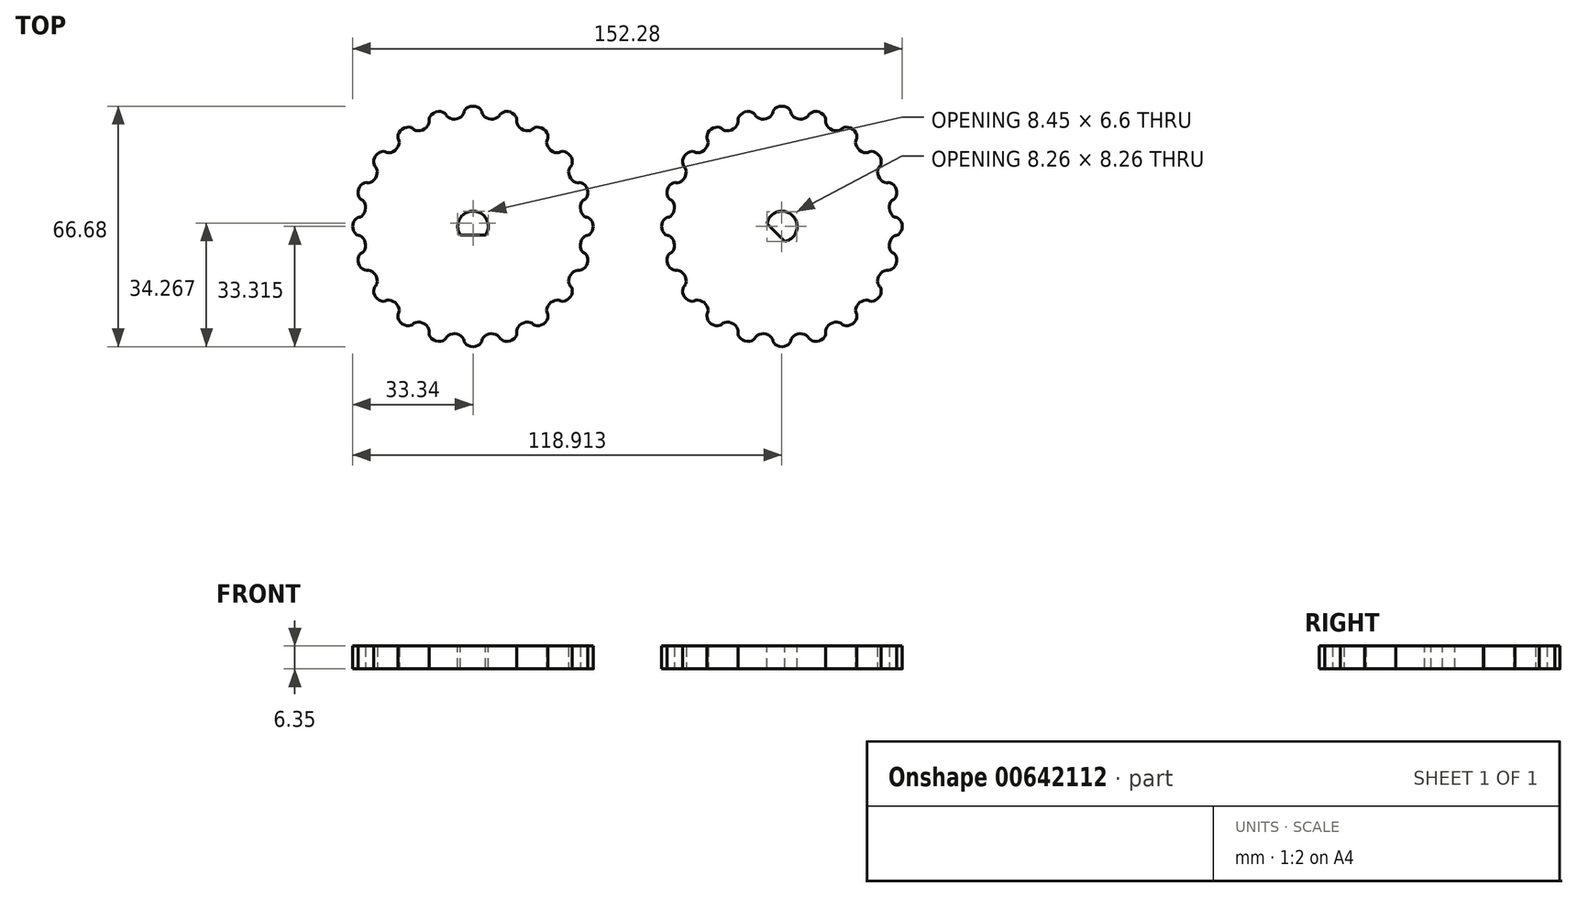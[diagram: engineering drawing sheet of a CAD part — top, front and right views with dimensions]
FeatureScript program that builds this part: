
annotation { "Feature Type Name" : "Feature", "Feature Type Description" : "" }
export const myFeature = defineFeature(function(context is Context, id is Id, definition is map)
    precondition{}
    {
        {
            assignVariable(context, id + "F0", {"name" : "PCD", "anyValue" : 2.5});
        }
        {
            assignVariable(context, id + "F1", {"name" : "SCD", "anyValue" : 1 / 16});
        }
        {
            assignVariable(context, id + "F2", {"name" : "Teeth", "anyValue" : .5 * getVariable(context, 'PCD') / getVariable(context, 'SCD')});
        }
        {
            var Q0;
            Q0=qCreatedBy(makeId("Top.planeOp"),FACE);
            var sketch = newSketch(context, id + "F3", { "sketchPlane" : qUnion([Q0])});
            skCircle(sketch, "E0", {"center": v(0, 0) * mm, "radius": 31.75 * mm, "construction": true});
            skCircle(sketch, "E1", {"center": v(0, 32.54) * mm, "radius": 0.8 * mm, "construction": true});
            skLineSegment(sketch, "E2", {"start": v(0, 33.34) * mm, "end": v(0, 32.54) * mm, "construction": true});
            skLineSegment(sketch, "E3", {"start": v(0, 0) * mm, "end": v(-4.84, 30.58) * mm, "construction": true});
            skCircle(sketch, "E4", {"center": v(-4.84, 30.58) * mm, "radius": 0.8 * mm, "construction": true});
            skLineSegment(sketch, "E5", {"start": v(0, 0) * mm, "end": v(0, 33.34) * mm, "construction": true});
            skCircle(sketch, "E6", {"center": v(0, 0) * mm, "radius": 33.34 * mm, "construction": true});
            skLineSegment(sketch, "E7", {"start": v(0, 0) * mm, "end": v(-2.5, 31.65) * mm, "construction": true});
            skLineSegment(sketch, "E8", {"start": v(0, 0) * mm, "end": v(-10.3, 31.7) * mm, "construction": true});
            skLineSegment(sketch, "E9", {"start": v(0, 0) * mm, "end": v(-7.41, 30.87) * mm, "construction": true});
            skCircle(sketch, "E10", {"center": v(-10.06, 30.95) * mm, "radius": 0.8 * mm, "construction": true});
            skCircle(sketch, "E11", {"center": v(-1.28, 32.52) * mm, "radius": 0.8 * mm, "construction": true});
            skCircle(sketch, "E12", {"center": v(-3.64, 30.74) * mm, "radius": 0.8 * mm, "construction": true});
            skLineSegment(sketch, "E13", {"start": v(-1.28, 32.52) * mm, "end": v(0, 0) * mm, "construction": true});
            skLineSegment(sketch, "E14", {"start": v(0, 0) * mm, "end": v(-3.64, 30.74) * mm, "construction": true});
            skLineSegment(sketch, "E15", {"start": v(-3.64, 30.74) * mm, "end": v(-2.85, 30.83) * mm, "construction": true});
            skLineSegment(sketch, "E16", {"start": v(-1.28, 32.52) * mm, "end": v(-2.07, 32.49) * mm, "construction": true});
            skPoint(sketch, "E17", {"position": v(-4.72, 29.8) * mm});
            skCircle(sketch, "E18", {"center": v(-6.04, 30.36) * mm, "radius": 0.8 * mm, "construction": true});
            skCircle(sketch, "E19", {"center": v(-8.83, 31.32) * mm, "radius": 0.8 * mm, "construction": true});
            skLineSegment(sketch, "E20", {"start": v(0, 0) * mm, "end": v(-6.04, 30.36) * mm, "construction": true});
            skLineSegment(sketch, "E21", {"start": v(0, 0) * mm, "end": v(-8.83, 31.32) * mm, "construction": true});
            skLineSegment(sketch, "E22", {"start": v(-6.04, 30.36) * mm, "end": v(-6.82, 30.2) * mm, "construction": true});
            skLineSegment(sketch, "E23", {"start": v(-8.83, 31.32) * mm, "end": v(-8.07, 31.54) * mm, "construction": true});
            skCircle(sketch, "E24", {"center": v(-0.64, 32.54) * mm, "radius": 0.8 * mm, "construction": true});
            skLineSegment(sketch, "E25", {"start": v(-0.64, 32.54) * mm, "end": v(0, 0) * mm, "construction": true});
            skCircle(sketch, "E26", {"center": v(-1.92, 32.49) * mm, "radius": 0.8 * mm, "construction": true});
            skLineSegment(sketch, "E27", {"start": v(-1.92, 32.49) * mm, "end": v(0, 0) * mm, "construction": true});
            skLineSegment(sketch, "E28", {"start": v(-0.64, 32.54) * mm, "end": v(-1.21, 33.09) * mm, "construction": true});
            skLineSegment(sketch, "E29", {"start": v(-1.92, 32.49) * mm, "end": v(-2.44, 31.9) * mm, "construction": true});
            skCircle(sketch, "E30", {"center": v(-3.03, 30.8) * mm, "radius": 0.8 * mm, "construction": true});
            skCircle(sketch, "E31", {"center": v(-4.24, 30.66) * mm, "radius": 0.8 * mm, "construction": true});
            skLineSegment(sketch, "E32", {"start": v(-3.03, 30.8) * mm, "end": v(0, 0) * mm, "construction": true});
            skLineSegment(sketch, "E33", {"start": v(-3.03, 30.8) * mm, "end": v(-2.53, 31.42) * mm, "construction": true});
            skLineSegment(sketch, "E34", {"start": v(-4.24, 30.66) * mm, "end": v(0, 0) * mm, "construction": true});
            skLineSegment(sketch, "E35", {"start": v(-4.24, 30.66) * mm, "end": v(-3.6, 30.19) * mm, "construction": true});
            skCircle(sketch, "E36", {"center": v(-5.44, 30.47) * mm, "radius": 0.8 * mm, "construction": true});
            skLineSegment(sketch, "E37", {"start": v(-5.44, 30.47) * mm, "end": v(0, 0) * mm, "construction": true});
            skLineSegment(sketch, "E38", {"start": v(-5.44, 30.47) * mm, "end": v(-5.9, 29.82) * mm, "construction": true});
            skCircle(sketch, "E39", {"center": v(-6.63, 30.24) * mm, "radius": 0.8 * mm, "construction": true});
            skCircle(sketch, "E40", {"center": v(-8.22, 31.49) * mm, "radius": 0.8 * mm, "construction": true});
            skCircle(sketch, "E41", {"center": v(-9.45, 31.14) * mm, "radius": 0.8 * mm, "construction": true});
            skLineSegment(sketch, "E42", {"start": v(-6.63, 30.24) * mm, "end": v(0, 0) * mm, "construction": true});
            skLineSegment(sketch, "E43", {"start": v(-6.63, 30.24) * mm, "end": v(-7.3, 30.66) * mm, "construction": true});
            skLineSegment(sketch, "E44", {"start": v(-8.22, 31.49) * mm, "end": v(0, 0) * mm, "construction": true});
            skLineSegment(sketch, "E45", {"start": v(-9.45, 31.14) * mm, "end": v(0, 0) * mm, "construction": true});
            skLineSegment(sketch, "E46", {"start": v(-8.22, 31.49) * mm, "end": v(-7.53, 31.09) * mm, "construction": true});
            skLineSegment(sketch, "E47", {"start": v(-9.45, 31.14) * mm, "end": v(-9.07, 31.84) * mm, "construction": true});
            skSolve(sketch);
        }
        {
            var Q0;
            Q0=qCreatedBy(makeId("Top.planeOp"),FACE);
            var sketch = newSketch(context, id + "F4", { "sketchPlane" : qUnion([Q0])});
            skPoint(sketch, "E48.0", {"position": v(0, 33.34) * mm});
            skPoint(sketch, "E48.1", {"position": v(-1.21, 33.09) * mm});
            skPoint(sketch, "E48.2", {"position": v(-2.07, 32.49) * mm});
            skPoint(sketch, "E48.3", {"position": v(-2.44, 31.9) * mm});
            skPoint(sketch, "E48.4", {"position": v(-2.5, 31.65) * mm});
            skPoint(sketch, "E48.5", {"position": v(-2.53, 31.42) * mm});
            skPoint(sketch, "E48.6", {"position": v(-2.85, 30.83) * mm});
            skPoint(sketch, "E48.7", {"position": v(-3.6, 30.19) * mm});
            skPoint(sketch, "E48.8", {"position": v(-4.72, 29.8) * mm});
            skPoint(sketch, "E48.9", {"position": v(-5.9, 29.82) * mm});
            skPoint(sketch, "E48.10", {"position": v(-6.82, 30.2) * mm});
            skPoint(sketch, "E48.11", {"position": v(-7.3, 30.66) * mm});
            skPoint(sketch, "E48.12", {"position": v(-7.41, 30.87) * mm});
            skPoint(sketch, "E48.13", {"position": v(-7.53, 31.09) * mm});
            skPoint(sketch, "E48.14", {"position": v(-8.07, 31.54) * mm});
            skPoint(sketch, "E48.15", {"position": v(-9.07, 31.84) * mm});
            skPoint(sketch, "E48.16", {"position": v(-10.3, 31.7) * mm});
            skLineSegment(sketch, "E49.0", {"start": v(0, 0) * mm, "end": v(0, 33.34) * mm});
            skLineSegment(sketch, "E49.1", {"start": v(0, 0) * mm, "end": v(-4.84, 30.58) * mm, "construction": true});
            skLineSegment(sketch, "E50.0", {"start": v(0, 0) * mm, "end": v(-10.3, 31.7) * mm});
            skPoint(sketch, "E51.1.1", {"position": v(-11.38, 31.1) * mm});
            skPoint(sketch, "E51.1.2", {"position": v(-12, 30.26) * mm});
            skPoint(sketch, "E51.1.3", {"position": v(-12.18, 29.58) * mm});
            skPoint(sketch, "E51.1.4", {"position": v(-12.15, 29.33) * mm});
            skPoint(sketch, "E51.1.5", {"position": v(-12.12, 29.1) * mm});
            skPoint(sketch, "E51.1.6", {"position": v(-12.24, 28.45) * mm});
            skPoint(sketch, "E51.1.7", {"position": v(-12.76, 27.6) * mm});
            skPoint(sketch, "E51.1.8", {"position": v(-13.7, 26.87) * mm});
            skPoint(sketch, "E51.1.9", {"position": v(-14.82, 26.54) * mm});
            skPoint(sketch, "E51.1.10", {"position": v(-15.82, 26.62) * mm});
            skPoint(sketch, "E51.1.11", {"position": v(-16.42, 26.9) * mm});
            skPoint(sketch, "E51.1.12", {"position": v(-16.59, 27.07) * mm});
            skPoint(sketch, "E51.1.13", {"position": v(-16.77, 27.24) * mm});
            skPoint(sketch, "E51.1.14", {"position": v(-17.42, 27.5) * mm});
            skPoint(sketch, "E51.1.15", {"position": v(-18.47, 27.48) * mm});
            skPoint(sketch, "E51.2.0", {"position": v(-19.6, 26.97) * mm});
            skPoint(sketch, "E51.2.1", {"position": v(-20.43, 26.06) * mm});
            skPoint(sketch, "E51.2.2", {"position": v(-20.77, 25.07) * mm});
            skPoint(sketch, "E51.2.3", {"position": v(-20.72, 24.37) * mm});
            skPoint(sketch, "E51.2.4", {"position": v(-20.62, 24.14) * mm});
            skPoint(sketch, "E51.2.5", {"position": v(-20.52, 23.93) * mm});
            skPoint(sketch, "E51.2.6", {"position": v(-20.43, 23.27) * mm});
            skPoint(sketch, "E51.2.7", {"position": v(-20.66, 22.3) * mm});
            skPoint(sketch, "E51.2.8", {"position": v(-21.33, 21.33) * mm});
            skPoint(sketch, "E51.2.9", {"position": v(-22.3, 20.66) * mm});
            skPoint(sketch, "E51.2.10", {"position": v(-23.27, 20.43) * mm});
            skPoint(sketch, "E51.2.11", {"position": v(-23.93, 20.52) * mm});
            skPoint(sketch, "E51.2.12", {"position": v(-24.14, 20.62) * mm});
            skPoint(sketch, "E51.2.13", {"position": v(-24.37, 20.72) * mm});
            skPoint(sketch, "E51.2.14", {"position": v(-25.07, 20.77) * mm});
            skPoint(sketch, "E51.2.15", {"position": v(-26.06, 20.43) * mm});
            skPoint(sketch, "E51.3.0", {"position": v(-26.97, 19.6) * mm});
            skPoint(sketch, "E51.3.1", {"position": v(-27.48, 18.47) * mm});
            skPoint(sketch, "E51.3.2", {"position": v(-27.5, 17.42) * mm});
            skPoint(sketch, "E51.3.3", {"position": v(-27.24, 16.77) * mm});
            skPoint(sketch, "E51.3.4", {"position": v(-27.07, 16.59) * mm});
            skPoint(sketch, "E51.3.5", {"position": v(-26.9, 16.42) * mm});
            skPoint(sketch, "E51.3.6", {"position": v(-26.62, 15.82) * mm});
            skPoint(sketch, "E51.3.7", {"position": v(-26.54, 14.82) * mm});
            skPoint(sketch, "E51.3.8", {"position": v(-26.87, 13.7) * mm});
            skPoint(sketch, "E51.3.9", {"position": v(-27.6, 12.76) * mm});
            skPoint(sketch, "E51.3.10", {"position": v(-28.45, 12.24) * mm});
            skPoint(sketch, "E51.3.11", {"position": v(-29.1, 12.12) * mm});
            skPoint(sketch, "E51.3.12", {"position": v(-29.33, 12.15) * mm});
            skPoint(sketch, "E51.3.13", {"position": v(-29.58, 12.18) * mm});
            skPoint(sketch, "E51.3.14", {"position": v(-30.26, 12) * mm});
            skPoint(sketch, "E51.3.15", {"position": v(-31.1, 11.38) * mm});
            skPoint(sketch, "E51.4.0", {"position": v(-31.7, 10.3) * mm});
            skPoint(sketch, "E51.4.1", {"position": v(-31.84, 9.07) * mm});
            skPoint(sketch, "E51.4.2", {"position": v(-31.54, 8.07) * mm});
            skPoint(sketch, "E51.4.3", {"position": v(-31.09, 7.53) * mm});
            skPoint(sketch, "E51.4.4", {"position": v(-30.87, 7.41) * mm});
            skPoint(sketch, "E51.4.5", {"position": v(-30.66, 7.3) * mm});
            skPoint(sketch, "E51.4.6", {"position": v(-30.2, 6.82) * mm});
            skPoint(sketch, "E51.4.7", {"position": v(-29.82, 5.9) * mm});
            skPoint(sketch, "E51.4.8", {"position": v(-29.8, 4.72) * mm});
            skPoint(sketch, "E51.4.9", {"position": v(-30.19, 3.6) * mm});
            skPoint(sketch, "E51.4.10", {"position": v(-30.83, 2.85) * mm});
            skPoint(sketch, "E51.4.11", {"position": v(-31.42, 2.53) * mm});
            skPoint(sketch, "E51.4.12", {"position": v(-31.65, 2.5) * mm});
            skPoint(sketch, "E51.4.13", {"position": v(-31.9, 2.44) * mm});
            skPoint(sketch, "E51.4.14", {"position": v(-32.49, 2.07) * mm});
            skPoint(sketch, "E51.4.15", {"position": v(-33.09, 1.21) * mm});
            skPoint(sketch, "E51.center", {"position": v(0, 0) * mm});
            skFitSpline(sketch, "E52", {"points": [v(0, 33.34) * mm, v(-1.21, 33.09) * mm, v(-2.07, 32.49) * mm, v(-2.44, 31.9) * mm, v(-2.5, 31.65) * mm, v(-2.53, 31.42) * mm, v(-2.85, 30.83) * mm, v(-3.6, 30.19) * mm, v(-4.72, 29.8) * mm, v(-5.9, 29.82) * mm, v(-6.82, 30.2) * mm, v(-7.3, 30.66) * mm, v(-7.41, 30.87) * mm, v(-7.53, 31.09) * mm, v(-8.07, 31.54) * mm, v(-9.07, 31.84) * mm, v(-10.3, 31.7) * mm, v(-11.38, 31.1) * mm, v(-12, 30.26) * mm, v(-12.18, 29.58) * mm, v(-12.15, 29.33) * mm, v(-12.12, 29.1) * mm, v(-12.24, 28.45) * mm, v(-12.76, 27.6) * mm, v(-13.7, 26.87) * mm, v(-14.82, 26.54) * mm, v(-15.82, 26.62) * mm, v(-16.42, 26.9) * mm, v(-16.59, 27.07) * mm, v(-16.77, 27.24) * mm, v(-17.42, 27.5) * mm, v(-18.47, 27.48) * mm, v(-19.6, 26.97) * mm, v(-20.43, 26.06) * mm, v(-20.77, 25.07) * mm, v(-20.72, 24.37) * mm, v(-20.62, 24.14) * mm, v(-20.52, 23.93) * mm, v(-20.43, 23.27) * mm, v(-20.66, 22.3) * mm, v(-21.33, 21.33) * mm, v(-22.3, 20.66) * mm, v(-23.27, 20.43) * mm, v(-23.93, 20.52) * mm, v(-24.14, 20.62) * mm, v(-24.37, 20.72) * mm, v(-25.07, 20.77) * mm, v(-26.06, 20.43) * mm, v(-26.97, 19.6) * mm, v(-27.48, 18.47) * mm, v(-27.5, 17.42) * mm, v(-27.24, 16.77) * mm, v(-27.07, 16.59) * mm, v(-26.9, 16.42) * mm, v(-26.62, 15.82) * mm, v(-26.54, 14.82) * mm, v(-26.87, 13.7) * mm, v(-27.6, 12.76) * mm, v(-28.45, 12.24) * mm, v(-29.1, 12.12) * mm, v(-29.33, 12.15) * mm, v(-29.58, 12.18) * mm, v(-30.26, 12) * mm, v(-28.33, 11.27) * mm, v(10.3, 31.7) * mm, v(9.07, 31.84) * mm, v(8.07, 31.54) * mm, v(7.53, 31.09) * mm, v(7.41, 30.87) * mm, v(7.3, 30.66) * mm, v(6.82, 30.2) * mm, v(5.9, 29.82) * mm, v(4.72, 29.8) * mm, v(3.6, 30.19) * mm, v(2.85, 30.83) * mm, v(2.53, 31.42) * mm, v(2.5, 31.65) * mm, v(2.44, 31.9) * mm, v(2.07, 32.49) * mm, v(1.21, 33.09) * mm, v(0, 33.34) * mm]});
            skArc(sketch, "E53", {"start": v(3.31, -2.4) * mm, "mid": v(0, 4.1) * mm, "end": v(-3.31, -2.4) * mm});
            skLineSegment(sketch, "E54", {"start": v(-3.31, -2.4) * mm, "end": v(3.31, -2.4) * mm});
            skLineSegment(sketch, "E55", {"start": v(0, 4.1) * mm, "end": v(4.77, 4.1) * mm, "construction": true});
            skPoint(sketch, "E56.0.5.0", {"position": v(-31.84, -9.07) * mm});
            skPoint(sketch, "E56.1.5.0", {"position": v(-33.09, -1.21) * mm});
            skPoint(sketch, "E56.2.5.0", {"position": v(-32.49, -2.07) * mm});
            skPoint(sketch, "E56.3.5.0", {"position": v(-31.9, -2.44) * mm});
            skPoint(sketch, "E56.4.5.0", {"position": v(-31.65, -2.5) * mm});
            skPoint(sketch, "E56.5.5.0", {"position": v(-31.42, -2.53) * mm});
            skPoint(sketch, "E56.6.5.0", {"position": v(-30.83, -2.85) * mm});
            skPoint(sketch, "E56.7.5.0", {"position": v(-30.19, -3.6) * mm});
            skPoint(sketch, "E56.8.5.0", {"position": v(-29.8, -4.72) * mm});
            skPoint(sketch, "E56.9.5.0", {"position": v(-29.82, -5.9) * mm});
            skPoint(sketch, "E56.10.5.0", {"position": v(-30.2, -6.82) * mm});
            skPoint(sketch, "E56.11.5.0", {"position": v(-30.66, -7.3) * mm});
            skPoint(sketch, "E56.12.5.0", {"position": v(-30.87, -7.41) * mm});
            skPoint(sketch, "E56.13.5.0", {"position": v(-31.09, -7.53) * mm});
            skPoint(sketch, "E56.14.5.0", {"position": v(-31.54, -8.07) * mm});
            skPoint(sketch, "E56.15.5.0", {"position": v(-33.34, 0) * mm});
            skPoint(sketch, "E56.0.6.0", {"position": v(-27.48, -18.47) * mm});
            skPoint(sketch, "E56.1.6.0", {"position": v(-31.1, -11.38) * mm});
            skPoint(sketch, "E56.2.6.0", {"position": v(-30.26, -12) * mm});
            skPoint(sketch, "E56.3.6.0", {"position": v(-29.58, -12.18) * mm});
            skPoint(sketch, "E56.4.6.0", {"position": v(-29.33, -12.15) * mm});
            skPoint(sketch, "E56.5.6.0", {"position": v(-29.1, -12.12) * mm});
            skPoint(sketch, "E56.6.6.0", {"position": v(-28.45, -12.24) * mm});
            skPoint(sketch, "E56.7.6.0", {"position": v(-27.6, -12.76) * mm});
            skPoint(sketch, "E56.8.6.0", {"position": v(-26.87, -13.7) * mm});
            skPoint(sketch, "E56.9.6.0", {"position": v(-26.54, -14.82) * mm});
            skPoint(sketch, "E56.10.6.0", {"position": v(-26.62, -15.82) * mm});
            skPoint(sketch, "E56.11.6.0", {"position": v(-26.9, -16.42) * mm});
            skPoint(sketch, "E56.12.6.0", {"position": v(-27.07, -16.59) * mm});
            skPoint(sketch, "E56.13.6.0", {"position": v(-27.24, -16.77) * mm});
            skPoint(sketch, "E56.14.6.0", {"position": v(-27.5, -17.42) * mm});
            skPoint(sketch, "E56.15.6.0", {"position": v(-31.7, -10.3) * mm});
            skPoint(sketch, "E56.0.7.0", {"position": v(-20.43, -26.06) * mm});
            skPoint(sketch, "E56.1.7.0", {"position": v(-26.06, -20.43) * mm});
            skPoint(sketch, "E56.2.7.0", {"position": v(-25.07, -20.77) * mm});
            skPoint(sketch, "E56.3.7.0", {"position": v(-24.37, -20.72) * mm});
            skPoint(sketch, "E56.4.7.0", {"position": v(-24.14, -20.62) * mm});
            skPoint(sketch, "E56.5.7.0", {"position": v(-23.93, -20.52) * mm});
            skPoint(sketch, "E56.6.7.0", {"position": v(-23.27, -20.43) * mm});
            skPoint(sketch, "E56.7.7.0", {"position": v(-22.3, -20.66) * mm});
            skPoint(sketch, "E56.8.7.0", {"position": v(-21.33, -21.33) * mm});
            skPoint(sketch, "E56.9.7.0", {"position": v(-20.66, -22.3) * mm});
            skPoint(sketch, "E56.10.7.0", {"position": v(-20.43, -23.27) * mm});
            skPoint(sketch, "E56.11.7.0", {"position": v(-20.52, -23.93) * mm});
            skPoint(sketch, "E56.12.7.0", {"position": v(-20.62, -24.14) * mm});
            skPoint(sketch, "E56.13.7.0", {"position": v(-20.72, -24.37) * mm});
            skPoint(sketch, "E56.14.7.0", {"position": v(-20.77, -25.07) * mm});
            skPoint(sketch, "E56.15.7.0", {"position": v(-26.97, -19.6) * mm});
            skPoint(sketch, "E56.0.8.0", {"position": v(-11.38, -31.1) * mm});
            skPoint(sketch, "E56.1.8.0", {"position": v(-18.47, -27.48) * mm});
            skPoint(sketch, "E56.2.8.0", {"position": v(-17.42, -27.5) * mm});
            skPoint(sketch, "E56.3.8.0", {"position": v(-16.77, -27.24) * mm});
            skPoint(sketch, "E56.4.8.0", {"position": v(-16.59, -27.07) * mm});
            skPoint(sketch, "E56.5.8.0", {"position": v(-16.42, -26.9) * mm});
            skPoint(sketch, "E56.6.8.0", {"position": v(-15.82, -26.62) * mm});
            skPoint(sketch, "E56.7.8.0", {"position": v(-14.82, -26.54) * mm});
            skPoint(sketch, "E56.8.8.0", {"position": v(-13.7, -26.87) * mm});
            skPoint(sketch, "E56.9.8.0", {"position": v(-12.76, -27.6) * mm});
            skPoint(sketch, "E56.10.8.0", {"position": v(-12.24, -28.45) * mm});
            skPoint(sketch, "E56.11.8.0", {"position": v(-12.12, -29.1) * mm});
            skPoint(sketch, "E56.12.8.0", {"position": v(-12.15, -29.33) * mm});
            skPoint(sketch, "E56.13.8.0", {"position": v(-12.18, -29.58) * mm});
            skPoint(sketch, "E56.14.8.0", {"position": v(-12, -30.26) * mm});
            skPoint(sketch, "E56.15.8.0", {"position": v(-19.6, -26.97) * mm});
            skPoint(sketch, "E56.0.9.0", {"position": v(-1.21, -33.09) * mm});
            skPoint(sketch, "E56.1.9.0", {"position": v(-9.07, -31.84) * mm});
            skPoint(sketch, "E56.2.9.0", {"position": v(-8.07, -31.54) * mm});
            skPoint(sketch, "E56.3.9.0", {"position": v(-7.53, -31.09) * mm});
            skPoint(sketch, "E56.4.9.0", {"position": v(-7.41, -30.87) * mm});
            skPoint(sketch, "E56.5.9.0", {"position": v(-7.3, -30.66) * mm});
            skPoint(sketch, "E56.6.9.0", {"position": v(-6.82, -30.2) * mm});
            skPoint(sketch, "E56.7.9.0", {"position": v(-5.9, -29.82) * mm});
            skPoint(sketch, "E56.8.9.0", {"position": v(-4.72, -29.8) * mm});
            skPoint(sketch, "E56.9.9.0", {"position": v(-3.6, -30.19) * mm});
            skPoint(sketch, "E56.10.9.0", {"position": v(-2.85, -30.83) * mm});
            skPoint(sketch, "E56.11.9.0", {"position": v(-2.53, -31.42) * mm});
            skPoint(sketch, "E56.12.9.0", {"position": v(-2.5, -31.65) * mm});
            skPoint(sketch, "E56.13.9.0", {"position": v(-2.44, -31.9) * mm});
            skPoint(sketch, "E56.14.9.0", {"position": v(-2.07, -32.49) * mm});
            skPoint(sketch, "E56.15.9.0", {"position": v(-10.3, -31.7) * mm});
            skPoint(sketch, "E56.0.10.0", {"position": v(9.07, -31.84) * mm});
            skPoint(sketch, "E56.1.10.0", {"position": v(1.21, -33.09) * mm});
            skPoint(sketch, "E56.2.10.0", {"position": v(2.07, -32.49) * mm});
            skPoint(sketch, "E56.3.10.0", {"position": v(2.44, -31.9) * mm});
            skPoint(sketch, "E56.4.10.0", {"position": v(2.5, -31.65) * mm});
            skPoint(sketch, "E56.5.10.0", {"position": v(2.53, -31.42) * mm});
            skPoint(sketch, "E56.6.10.0", {"position": v(2.85, -30.83) * mm});
            skPoint(sketch, "E56.7.10.0", {"position": v(3.6, -30.19) * mm});
            skPoint(sketch, "E56.8.10.0", {"position": v(4.72, -29.8) * mm});
            skPoint(sketch, "E56.9.10.0", {"position": v(5.9, -29.82) * mm});
            skPoint(sketch, "E56.10.10.0", {"position": v(6.82, -30.2) * mm});
            skPoint(sketch, "E56.11.10.0", {"position": v(7.3, -30.66) * mm});
            skPoint(sketch, "E56.12.10.0", {"position": v(7.41, -30.87) * mm});
            skPoint(sketch, "E56.13.10.0", {"position": v(7.53, -31.09) * mm});
            skPoint(sketch, "E56.14.10.0", {"position": v(8.07, -31.54) * mm});
            skPoint(sketch, "E56.15.10.0", {"position": v(0, -33.34) * mm});
            skPoint(sketch, "E56.0.11.0", {"position": v(18.47, -27.48) * mm});
            skPoint(sketch, "E56.1.11.0", {"position": v(11.38, -31.1) * mm});
            skPoint(sketch, "E56.2.11.0", {"position": v(12, -30.26) * mm});
            skPoint(sketch, "E56.3.11.0", {"position": v(12.18, -29.58) * mm});
            skPoint(sketch, "E56.4.11.0", {"position": v(12.15, -29.33) * mm});
            skPoint(sketch, "E56.5.11.0", {"position": v(12.12, -29.1) * mm});
            skPoint(sketch, "E56.6.11.0", {"position": v(12.24, -28.45) * mm});
            skPoint(sketch, "E56.7.11.0", {"position": v(12.76, -27.6) * mm});
            skPoint(sketch, "E56.8.11.0", {"position": v(13.7, -26.87) * mm});
            skPoint(sketch, "E56.9.11.0", {"position": v(14.82, -26.54) * mm});
            skPoint(sketch, "E56.10.11.0", {"position": v(15.82, -26.62) * mm});
            skPoint(sketch, "E56.11.11.0", {"position": v(16.42, -26.9) * mm});
            skPoint(sketch, "E56.12.11.0", {"position": v(16.59, -27.07) * mm});
            skPoint(sketch, "E56.13.11.0", {"position": v(16.77, -27.24) * mm});
            skPoint(sketch, "E56.14.11.0", {"position": v(17.42, -27.5) * mm});
            skPoint(sketch, "E56.15.11.0", {"position": v(10.3, -31.7) * mm});
            skPoint(sketch, "E56.0.12.0", {"position": v(26.06, -20.43) * mm});
            skPoint(sketch, "E56.1.12.0", {"position": v(20.43, -26.06) * mm});
            skPoint(sketch, "E56.2.12.0", {"position": v(20.77, -25.07) * mm});
            skPoint(sketch, "E56.3.12.0", {"position": v(20.72, -24.37) * mm});
            skPoint(sketch, "E56.4.12.0", {"position": v(20.62, -24.14) * mm});
            skPoint(sketch, "E56.5.12.0", {"position": v(20.52, -23.93) * mm});
            skPoint(sketch, "E56.6.12.0", {"position": v(20.43, -23.27) * mm});
            skPoint(sketch, "E56.7.12.0", {"position": v(20.66, -22.3) * mm});
            skPoint(sketch, "E56.8.12.0", {"position": v(21.33, -21.33) * mm});
            skPoint(sketch, "E56.9.12.0", {"position": v(22.3, -20.66) * mm});
            skPoint(sketch, "E56.10.12.0", {"position": v(23.27, -20.43) * mm});
            skPoint(sketch, "E56.11.12.0", {"position": v(23.93, -20.52) * mm});
            skPoint(sketch, "E56.12.12.0", {"position": v(24.14, -20.62) * mm});
            skPoint(sketch, "E56.13.12.0", {"position": v(24.37, -20.72) * mm});
            skPoint(sketch, "E56.14.12.0", {"position": v(25.07, -20.77) * mm});
            skPoint(sketch, "E56.15.12.0", {"position": v(19.6, -26.97) * mm});
            skPoint(sketch, "E56.0.13.0", {"position": v(31.1, -11.38) * mm});
            skPoint(sketch, "E56.1.13.0", {"position": v(27.48, -18.47) * mm});
            skPoint(sketch, "E56.2.13.0", {"position": v(27.5, -17.42) * mm});
            skPoint(sketch, "E56.3.13.0", {"position": v(27.24, -16.77) * mm});
            skPoint(sketch, "E56.4.13.0", {"position": v(27.07, -16.59) * mm});
            skPoint(sketch, "E56.5.13.0", {"position": v(26.9, -16.42) * mm});
            skPoint(sketch, "E56.6.13.0", {"position": v(26.62, -15.82) * mm});
            skPoint(sketch, "E56.7.13.0", {"position": v(26.54, -14.82) * mm});
            skPoint(sketch, "E56.8.13.0", {"position": v(26.87, -13.7) * mm});
            skPoint(sketch, "E56.9.13.0", {"position": v(27.6, -12.76) * mm});
            skPoint(sketch, "E56.10.13.0", {"position": v(28.45, -12.24) * mm});
            skPoint(sketch, "E56.11.13.0", {"position": v(29.1, -12.12) * mm});
            skPoint(sketch, "E56.12.13.0", {"position": v(29.33, -12.15) * mm});
            skPoint(sketch, "E56.13.13.0", {"position": v(29.58, -12.18) * mm});
            skPoint(sketch, "E56.14.13.0", {"position": v(30.26, -12) * mm});
            skPoint(sketch, "E56.15.13.0", {"position": v(26.97, -19.6) * mm});
            skPoint(sketch, "E56.0.14.0", {"position": v(33.09, -1.21) * mm});
            skPoint(sketch, "E56.1.14.0", {"position": v(31.84, -9.07) * mm});
            skPoint(sketch, "E56.2.14.0", {"position": v(31.54, -8.07) * mm});
            skPoint(sketch, "E56.3.14.0", {"position": v(31.09, -7.53) * mm});
            skPoint(sketch, "E56.4.14.0", {"position": v(30.87, -7.41) * mm});
            skPoint(sketch, "E56.5.14.0", {"position": v(30.66, -7.3) * mm});
            skPoint(sketch, "E56.6.14.0", {"position": v(30.2, -6.82) * mm});
            skPoint(sketch, "E56.7.14.0", {"position": v(29.82, -5.9) * mm});
            skPoint(sketch, "E56.8.14.0", {"position": v(29.8, -4.72) * mm});
            skPoint(sketch, "E56.9.14.0", {"position": v(30.19, -3.6) * mm});
            skPoint(sketch, "E56.10.14.0", {"position": v(30.83, -2.85) * mm});
            skPoint(sketch, "E56.11.14.0", {"position": v(31.42, -2.53) * mm});
            skPoint(sketch, "E56.12.14.0", {"position": v(31.65, -2.5) * mm});
            skPoint(sketch, "E56.13.14.0", {"position": v(31.9, -2.44) * mm});
            skPoint(sketch, "E56.14.14.0", {"position": v(32.49, -2.07) * mm});
            skPoint(sketch, "E56.15.14.0", {"position": v(31.7, -10.3) * mm});
            skPoint(sketch, "E56.0.15.0", {"position": v(31.84, 9.07) * mm});
            skPoint(sketch, "E56.1.15.0", {"position": v(33.09, 1.21) * mm});
            skPoint(sketch, "E56.2.15.0", {"position": v(32.49, 2.07) * mm});
            skPoint(sketch, "E56.3.15.0", {"position": v(31.9, 2.44) * mm});
            skPoint(sketch, "E56.4.15.0", {"position": v(31.65, 2.5) * mm});
            skPoint(sketch, "E56.5.15.0", {"position": v(31.42, 2.53) * mm});
            skPoint(sketch, "E56.6.15.0", {"position": v(30.83, 2.85) * mm});
            skPoint(sketch, "E56.7.15.0", {"position": v(30.19, 3.6) * mm});
            skPoint(sketch, "E56.8.15.0", {"position": v(29.8, 4.72) * mm});
            skPoint(sketch, "E56.9.15.0", {"position": v(29.82, 5.9) * mm});
            skPoint(sketch, "E56.10.15.0", {"position": v(30.2, 6.82) * mm});
            skPoint(sketch, "E56.11.15.0", {"position": v(30.66, 7.3) * mm});
            skPoint(sketch, "E56.12.15.0", {"position": v(30.87, 7.41) * mm});
            skPoint(sketch, "E56.13.15.0", {"position": v(31.09, 7.53) * mm});
            skPoint(sketch, "E56.14.15.0", {"position": v(31.54, 8.07) * mm});
            skPoint(sketch, "E56.15.15.0", {"position": v(33.34, 0) * mm});
            skPoint(sketch, "E56.0.16.0", {"position": v(27.48, 18.47) * mm});
            skPoint(sketch, "E56.1.16.0", {"position": v(31.1, 11.38) * mm});
            skPoint(sketch, "E56.2.16.0", {"position": v(30.26, 12) * mm});
            skPoint(sketch, "E56.3.16.0", {"position": v(29.58, 12.18) * mm});
            skPoint(sketch, "E56.4.16.0", {"position": v(29.33, 12.15) * mm});
            skPoint(sketch, "E56.5.16.0", {"position": v(29.1, 12.12) * mm});
            skPoint(sketch, "E56.6.16.0", {"position": v(28.45, 12.24) * mm});
            skPoint(sketch, "E56.7.16.0", {"position": v(27.6, 12.76) * mm});
            skPoint(sketch, "E56.8.16.0", {"position": v(26.87, 13.7) * mm});
            skPoint(sketch, "E56.9.16.0", {"position": v(26.54, 14.82) * mm});
            skPoint(sketch, "E56.10.16.0", {"position": v(26.62, 15.82) * mm});
            skPoint(sketch, "E56.11.16.0", {"position": v(26.9, 16.42) * mm});
            skPoint(sketch, "E56.12.16.0", {"position": v(27.07, 16.59) * mm});
            skPoint(sketch, "E56.13.16.0", {"position": v(27.24, 16.77) * mm});
            skPoint(sketch, "E56.14.16.0", {"position": v(27.5, 17.42) * mm});
            skPoint(sketch, "E56.15.16.0", {"position": v(31.7, 10.3) * mm});
            skPoint(sketch, "E56.0.17.0", {"position": v(20.43, 26.06) * mm});
            skPoint(sketch, "E56.1.17.0", {"position": v(26.06, 20.43) * mm});
            skPoint(sketch, "E56.2.17.0", {"position": v(25.07, 20.77) * mm});
            skPoint(sketch, "E56.3.17.0", {"position": v(24.37, 20.72) * mm});
            skPoint(sketch, "E56.4.17.0", {"position": v(24.14, 20.62) * mm});
            skPoint(sketch, "E56.5.17.0", {"position": v(23.93, 20.52) * mm});
            skPoint(sketch, "E56.6.17.0", {"position": v(23.27, 20.43) * mm});
            skPoint(sketch, "E56.7.17.0", {"position": v(22.3, 20.66) * mm});
            skPoint(sketch, "E56.8.17.0", {"position": v(21.33, 21.33) * mm});
            skPoint(sketch, "E56.9.17.0", {"position": v(20.66, 22.3) * mm});
            skPoint(sketch, "E56.10.17.0", {"position": v(20.43, 23.27) * mm});
            skPoint(sketch, "E56.11.17.0", {"position": v(20.52, 23.93) * mm});
            skPoint(sketch, "E56.12.17.0", {"position": v(20.62, 24.14) * mm});
            skPoint(sketch, "E56.13.17.0", {"position": v(20.72, 24.37) * mm});
            skPoint(sketch, "E56.14.17.0", {"position": v(20.77, 25.07) * mm});
            skPoint(sketch, "E56.15.17.0", {"position": v(26.97, 19.6) * mm});
            skPoint(sketch, "E56.0.18.0", {"position": v(11.38, 31.1) * mm});
            skPoint(sketch, "E56.1.18.0", {"position": v(18.47, 27.48) * mm});
            skPoint(sketch, "E56.2.18.0", {"position": v(17.42, 27.5) * mm});
            skPoint(sketch, "E56.3.18.0", {"position": v(16.77, 27.24) * mm});
            skPoint(sketch, "E56.4.18.0", {"position": v(16.59, 27.07) * mm});
            skPoint(sketch, "E56.5.18.0", {"position": v(16.42, 26.9) * mm});
            skPoint(sketch, "E56.6.18.0", {"position": v(15.82, 26.62) * mm});
            skPoint(sketch, "E56.7.18.0", {"position": v(14.82, 26.54) * mm});
            skPoint(sketch, "E56.8.18.0", {"position": v(13.7, 26.87) * mm});
            skPoint(sketch, "E56.9.18.0", {"position": v(12.76, 27.6) * mm});
            skPoint(sketch, "E56.10.18.0", {"position": v(12.24, 28.45) * mm});
            skPoint(sketch, "E56.11.18.0", {"position": v(12.12, 29.1) * mm});
            skPoint(sketch, "E56.12.18.0", {"position": v(12.15, 29.33) * mm});
            skPoint(sketch, "E56.13.18.0", {"position": v(12.18, 29.58) * mm});
            skPoint(sketch, "E56.14.18.0", {"position": v(12, 30.26) * mm});
            skPoint(sketch, "E56.15.18.0", {"position": v(19.6, 26.97) * mm});
            skSolve(sketch);
        }
        {
            var Q0;
            {var subQ0=sQuery(id+"F4.wireOp",EDGE,"E52");var subQ1=sQuery(id+"F4.wireOp",EDGE,"E49.0");var subQ2=makeQuery(id+"F4.imprint","INTERSECT",VERTEX,{"disambiguationData":[OD(0.0)],"derivedFrom":[subQ1,subQ0]});Q0=makeQuery(id+"F4.imprint","IMPRINT",FACE,{"disambiguationData":[TD([[makeQuery(id+"F4.imprint","IMPRINT",EDGE,{"disambiguationData":[TD([[subQ2,1.0]])],"derivedFrom":subQ1}),1.0]])]});}
            var Q1;
            {var subQ0=sQuery(id+"F4.wireOp",EDGE,"E53");var subQ1=sQuery(id+"F4.wireOp",EDGE,"E49.0");var subQ2=makeQuery(id+"F4.imprint","INTERSECT",VERTEX,{"derivedFrom":[subQ1,subQ0]});Q1=makeQuery(id+"F4.imprint","IMPRINT",FACE,{"disambiguationData":[TD([[makeQuery(id+"F4.imprint","IMPRINT",EDGE,{"disambiguationData":[TD([[subQ2,-1.0]])],"derivedFrom":subQ1}),1.0]])]});}
            var Q2;
            {var subQ0=sQuery(id+"F4.wireOp",EDGE,"E50.0");var subQ1=sQuery(id+"F4.wireOp",EDGE,"E49.0");var subQ2=makeQuery(id+"F4.imprint","INTERSECT",VERTEX,{"derivedFrom":[subQ1,subQ0]});Q2=makeQuery(id+"F4.imprint","IMPRINT",FACE,{"disambiguationData":[TD([[makeQuery(id+"F4.imprint","IMPRINT",EDGE,{"disambiguationData":[TD([[subQ2,-1.0]])],"derivedFrom":subQ1}),1.0]])]});}
            extrude(context, id + "F5", {"entities" : qUnion([Q0, Q1, Q2]), "depth" : 6.35 * mm, "offsetDistance" : 25.4 * mm});
        }
        {
            var Q0;
            Q0=makeQuery(id+"F5.opExtrude","SWEPT_BODY",BODY,{"disambiguationData":[OSD([sQuery(id+"F4.wireOp",EDGE,"E49.0"),sQuery(id+"F4.wireOp",EDGE,"E50.0"),sQuery(id+"F4.wireOp",EDGE,"E52")])]});
            var Q1;
            Q1=makeQuery(id+"F5.opExtrude","SWEPT_EDGE",EDGE,{"disambiguationData":[OSD([sQuery(id+"F4.wireOp",EDGE,"E49.0"),sQuery(id+"F4.wireOp",EDGE,"E50.0")])]});
            circularPattern(context, id + "F6", {"operationType" : NewBodyOperationType.ADD, "entities" : qUnion([Q0]), "axis" : qUnion([Q1]), "angle" : 360 * degree, "instanceCount" : getVariable(context, 'Teeth'), "equalSpace" : true});
        }
        {
            var Q0;
            Q0=makeQuery(id+"F5.opExtrude","SWEPT_BODY",BODY,{"disambiguationData":[OSD([sQuery(id+"F4.wireOp",EDGE,"E49.0"),sQuery(id+"F4.wireOp",EDGE,"E50.0"),sQuery(id+"F4.wireOp",EDGE,"E52")])]});
            transform(context, id + "F7", {"entities" : qUnion([Q0]), "transformType" : TransformType.TRANSLATION_3D, "dx" : 85.6 * mm, "dy" : 0 * mm, "dz" : 0 * mm, "makeCopy" : true});
        }
        {
            var Q0;
            {var subQ0=makeQuery(id+"F5.opExtrude","CAP_FACE",FACE,{"disambiguationData":[OSD([sQuery(id+"F4.wireOp",EDGE,"E49.0"),sQuery(id+"F4.wireOp",EDGE,"E50.0"),sQuery(id+"F4.wireOp",EDGE,"E52")])],"isStart":false});Q0=makeQuery(id+"F6.boolean.opBoolean","MERGE",FACE,{"derivedFrom":[subQ0,makeQuery(id+"F6.opPattern","COPY",FACE,{"derivedFrom":subQ0,"instanceName":"1"}),makeQuery(id+"F6.opPattern","COPY",FACE,{"derivedFrom":subQ0,"instanceName":"2"}),makeQuery(id+"F6.opPattern","COPY",FACE,{"derivedFrom":subQ0,"instanceName":"3"}),makeQuery(id+"F6.opPattern","COPY",FACE,{"derivedFrom":subQ0,"instanceName":"4"}),makeQuery(id+"F6.opPattern","COPY",FACE,{"derivedFrom":subQ0,"instanceName":"5"}),makeQuery(id+"F6.opPattern","COPY",FACE,{"derivedFrom":subQ0,"instanceName":"6"}),makeQuery(id+"F6.opPattern","COPY",FACE,{"derivedFrom":subQ0,"instanceName":"7"}),makeQuery(id+"F6.opPattern","COPY",FACE,{"derivedFrom":subQ0,"instanceName":"8"}),makeQuery(id+"F6.opPattern","COPY",FACE,{"derivedFrom":subQ0,"instanceName":"9"}),makeQuery(id+"F6.opPattern","COPY",FACE,{"derivedFrom":subQ0,"instanceName":"10"}),makeQuery(id+"F6.opPattern","COPY",FACE,{"derivedFrom":subQ0,"instanceName":"11"}),makeQuery(id+"F6.opPattern","COPY",FACE,{"derivedFrom":subQ0,"instanceName":"12"}),makeQuery(id+"F6.opPattern","COPY",FACE,{"derivedFrom":subQ0,"instanceName":"13"}),makeQuery(id+"F6.opPattern","COPY",FACE,{"derivedFrom":subQ0,"instanceName":"14"}),makeQuery(id+"F6.opPattern","COPY",FACE,{"derivedFrom":subQ0,"instanceName":"15"}),makeQuery(id+"F6.opPattern","COPY",FACE,{"derivedFrom":subQ0,"instanceName":"16"}),makeQuery(id+"F6.opPattern","COPY",FACE,{"derivedFrom":subQ0,"instanceName":"17"}),makeQuery(id+"F6.opPattern","COPY",FACE,{"derivedFrom":subQ0,"instanceName":"18"}),makeQuery(id+"F6.opPattern","COPY",FACE,{"derivedFrom":subQ0,"instanceName":"19"})]});}
            var sketch = newSketch(context, id + "F8", { "sketchPlane" : qUnion([Q0])});
            skCircle(sketch, "E57", {"center": v(0, 0) * mm, "radius": 4.23 * mm});
            skLineSegment(sketch, "E58", {"start": v(3.5, -2.37) * mm, "end": v(-3.5, -2.37) * mm});
            skSolve(sketch);
        }
        {
            var Q0;
            {var subQ0=sQuery(id+"F8.wireOp",EDGE,"E58");Q0=makeQuery(id+"F8.imprint","IMPRINT",FACE,{"disambiguationData":[TD([[makeQuery(id+"F8.imprint","IMPRINT",EDGE,{"derivedFrom":subQ0}),-1.0]])]});}
            extrude(context, id + "F9", {"entities" : qUnion([Q0]), "operationType" : NewBodyOperationType.REMOVE, "oppositeDirection" : true, "depth" : 25.4 * mm, "offsetDistance" : 25.4 * mm});
        }
        {
            var Q0;
            {var subQ0=makeQuery(id+"F5.opExtrude","CAP_FACE",FACE,{"disambiguationData":[OSD([sQuery(id+"F4.wireOp",EDGE,"E49.0"),sQuery(id+"F4.wireOp",EDGE,"E50.0"),sQuery(id+"F4.wireOp",EDGE,"E52")])],"isStart":false});Q0=makeQuery(id+"F7.opPattern","COPY",FACE,{"derivedFrom":makeQuery(id+"F6.boolean.opBoolean","MERGE",FACE,{"derivedFrom":[subQ0,makeQuery(id+"F6.opPattern","COPY",FACE,{"derivedFrom":subQ0,"instanceName":"1"}),makeQuery(id+"F6.opPattern","COPY",FACE,{"derivedFrom":subQ0,"instanceName":"2"}),makeQuery(id+"F6.opPattern","COPY",FACE,{"derivedFrom":subQ0,"instanceName":"3"}),makeQuery(id+"F6.opPattern","COPY",FACE,{"derivedFrom":subQ0,"instanceName":"4"}),makeQuery(id+"F6.opPattern","COPY",FACE,{"derivedFrom":subQ0,"instanceName":"5"}),makeQuery(id+"F6.opPattern","COPY",FACE,{"derivedFrom":subQ0,"instanceName":"6"}),makeQuery(id+"F6.opPattern","COPY",FACE,{"derivedFrom":subQ0,"instanceName":"7"}),makeQuery(id+"F6.opPattern","COPY",FACE,{"derivedFrom":subQ0,"instanceName":"8"}),makeQuery(id+"F6.opPattern","COPY",FACE,{"derivedFrom":subQ0,"instanceName":"9"}),makeQuery(id+"F6.opPattern","COPY",FACE,{"derivedFrom":subQ0,"instanceName":"10"}),makeQuery(id+"F6.opPattern","COPY",FACE,{"derivedFrom":subQ0,"instanceName":"11"}),makeQuery(id+"F6.opPattern","COPY",FACE,{"derivedFrom":subQ0,"instanceName":"12"}),makeQuery(id+"F6.opPattern","COPY",FACE,{"derivedFrom":subQ0,"instanceName":"13"}),makeQuery(id+"F6.opPattern","COPY",FACE,{"derivedFrom":subQ0,"instanceName":"14"}),makeQuery(id+"F6.opPattern","COPY",FACE,{"derivedFrom":subQ0,"instanceName":"15"}),makeQuery(id+"F6.opPattern","COPY",FACE,{"derivedFrom":subQ0,"instanceName":"16"}),makeQuery(id+"F6.opPattern","COPY",FACE,{"derivedFrom":subQ0,"instanceName":"17"}),makeQuery(id+"F6.opPattern","COPY",FACE,{"derivedFrom":subQ0,"instanceName":"18"}),makeQuery(id+"F6.opPattern","COPY",FACE,{"derivedFrom":subQ0,"instanceName":"19"})]}),"instanceName":"1"});}
            var sketch = newSketch(context, id + "F10", { "sketchPlane" : qUnion([Q0])});
            skCircle(sketch, "E59", {"center": v(85.6, 0) * mm, "radius": 4.23 * mm});
            skLineSegment(sketch, "E60", {"start": v(86.4, -4.15) * mm, "end": v(81.44, 0.8) * mm});
            skLineSegment(sketch, "E61", {"start": v(85.6, 33.34) * mm, "end": v(85.6, -33.34) * mm, "construction": true});
            skLineSegment(sketch, "E62", {"start": v(52.26, 0) * mm, "end": v(118.94, 0) * mm, "construction": true});
            skLineSegment(sketch, "E63", {"start": v(85.6, 0) * mm, "end": v(62.46, -23.14) * mm, "construction": true});
            skSolve(sketch);
        }
        {
            var Q0;
            {var subQ0=sQuery(id+"F10.wireOp",EDGE,"E60");Q0=makeQuery(id+"F10.imprint","IMPRINT",FACE,{"disambiguationData":[TD([[makeQuery(id+"F10.imprint","IMPRINT",EDGE,{"derivedFrom":subQ0}),-1.0]])]});}
            extrude(context, id + "F11", {"entities" : qUnion([Q0]), "operationType" : NewBodyOperationType.REMOVE, "endBound" : BoundingType.THROUGH_ALL, "oppositeDirection" : true, "depth" : 25.4 * mm, "offsetDistance" : 25.4 * mm});
        }
    });
